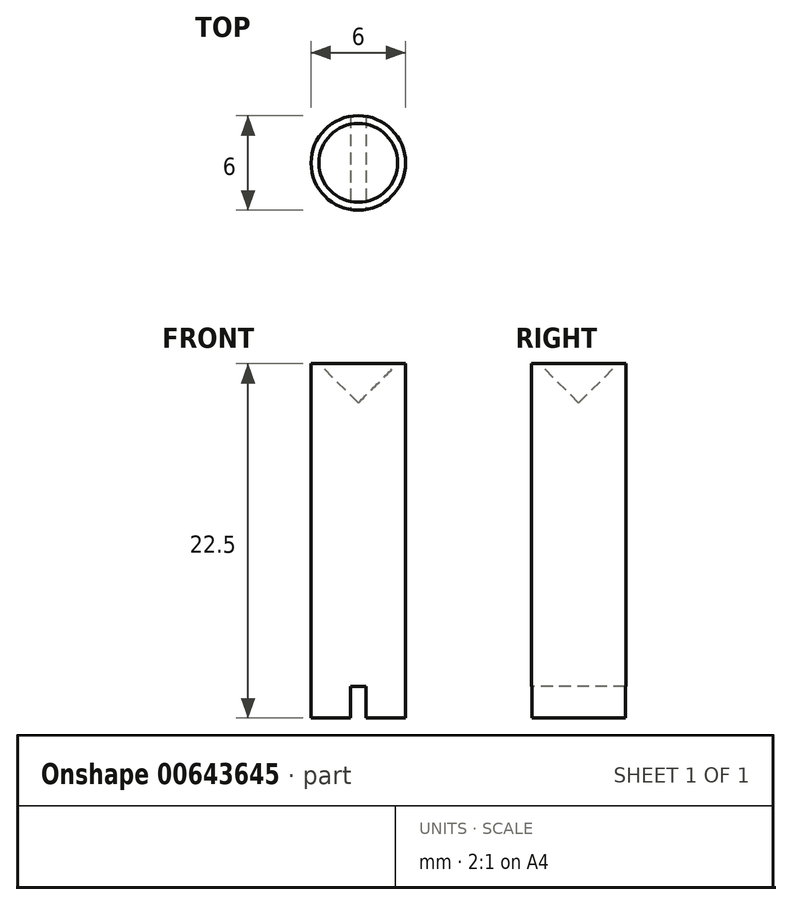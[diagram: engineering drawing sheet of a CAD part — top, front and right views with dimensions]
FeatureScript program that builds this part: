
annotation { "Feature Type Name" : "Feature", "Feature Type Description" : "" }
export const myFeature = defineFeature(function(context is Context, id is Id, definition is map)
    precondition{}
    {
        {
            var Q0;
            Q0=qCreatedBy(makeId("Front.planeOp"),FACE);
            var sketch = newSketch(context, id + "F0", { "sketchPlane" : qUnion([Q0])});
            skLineSegment(sketch, "E0", {"start": v(0, 0) * mm, "end": v(-3, 0) * mm});
            skLineSegment(sketch, "E1", {"start": v(-3, 0) * mm, "end": v(-3, 22.5) * mm});
            skLineSegment(sketch, "E2", {"start": v(-3, 22.5) * mm, "end": v(-2.5, 22.5) * mm});
            skLineSegment(sketch, "E3", {"start": v(-2.5, 22.5) * mm, "end": v(0, 20) * mm});
            skLineSegment(sketch, "E4", {"start": v(0, 20) * mm, "end": v(0, 0) * mm});
            skSolve(sketch);
        }
        {
            var Q0;
            Q0 = qSketchRegion(id + "F0", true);
            var Q1;
            Q1=sQuery(id+"F0.wireOp",EDGE,"E4");
            revolve(context, id + "F1", {"entities" : qUnion([Q0]), "axis" : qUnion([Q1]), "revolveType" : RevolveType.FULL});
        }
        {
            var Q0;
            Q0=makeQuery(id+"F1.opRevolve","SWEPT_FACE",FACE,{"disambiguationData":[OSD([sQuery(id+"F0.wireOp",EDGE,"E0")])]});
            var sketch = newSketch(context, id + "F2", { "sketchPlane" : qUnion([Q0])});
            skLineSegment(sketch, "E5.bottom", {"start": v(0.5, -4.74) * mm, "end": v(-0.5, -4.74) * mm});
            skLineSegment(sketch, "E5.top", {"start": v(0.5, 4.74) * mm, "end": v(-0.5, 4.74) * mm});
            skLineSegment(sketch, "E5.left", {"start": v(0.5, -4.74) * mm, "end": v(0.5, 4.74) * mm});
            skLineSegment(sketch, "E5.right", {"start": v(-0.5, -4.74) * mm, "end": v(-0.5, 4.74) * mm});
            skPoint(sketch, "E5.middle", {"position": v(0, 0) * mm});
            skSolve(sketch);
        }
        {
            var Q0;
            Q0 = qSketchRegion(id + "F2", true);
            extrude(context, id + "F3", {"entities" : qUnion([Q0]), "operationType" : NewBodyOperationType.REMOVE, "oppositeDirection" : true, "depth" : 2 * mm, "offsetDistance" : 25 * mm});
        }
    });
